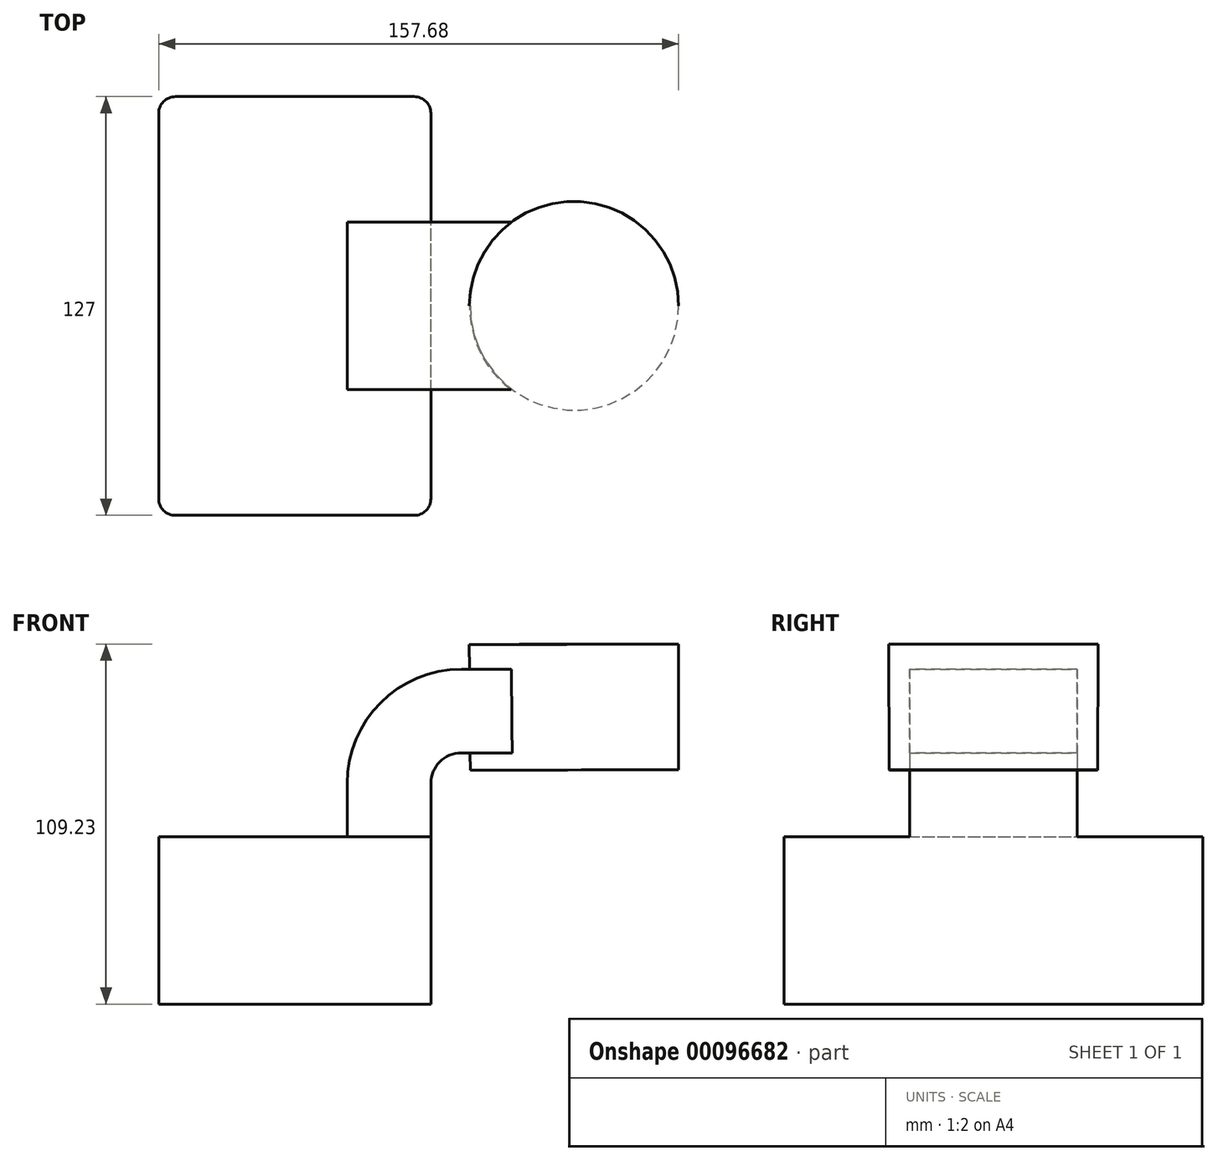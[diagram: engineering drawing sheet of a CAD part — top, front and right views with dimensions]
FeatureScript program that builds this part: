
annotation { "Feature Type Name" : "Feature", "Feature Type Description" : "" }
export const myFeature = defineFeature(function(context is Context, id is Id, definition is map)
    precondition{}
    {
        {
            var Q0;
            Q0=qCreatedBy(makeId("Front.planeOp"),FACE);
            var sketch = newSketch(context, id + "F0", { "sketchPlane" : qUnion([Q0])});
            skLineSegment(sketch, "E0.bottom", {"start": v(41.28, -25.4) * mm, "end": v(-41.27, -25.4) * mm});
            skLineSegment(sketch, "E0.top", {"start": v(41.27, 25.4) * mm, "end": v(-41.28, 25.4) * mm});
            skLineSegment(sketch, "E0.left", {"start": v(41.28, -25.4) * mm, "end": v(41.28, 25.4) * mm});
            skLineSegment(sketch, "E0.right", {"start": v(-41.27, -25.4) * mm, "end": v(-41.28, 25.4) * mm});
            skPoint(sketch, "E0.middle", {"position": v(0, 0) * mm});
            skLineSegment(sketch, "E1.bottom", {"start": v(116.41, 45.73) * mm, "end": v(52.91, 45.73) * mm});
            skLineSegment(sketch, "E1.top", {"start": v(116.41, 83.83) * mm, "end": v(52.91, 83.83) * mm});
            skLineSegment(sketch, "E1.left", {"start": v(116.41, 45.73) * mm, "end": v(116.41, 83.83) * mm});
            skLineSegment(sketch, "E1.right", {"start": v(52.91, 45.73) * mm, "end": v(52.91, 83.83) * mm});
            skPoint(sketch, "E1.middle", {"position": v(84.66, 64.78) * mm});
            skLineSegment(sketch, "E2", {"start": v(41.27, 25.4) * mm, "end": v(41.27, 41.48) * mm});
            skArc(sketch, "E3", {"start": v(41.27, 41.48) * mm, "mid": v(44, 48.07) * mm, "end": v(50.6, 50.8) * mm});
            skLineSegment(sketch, "E4", {"start": v(50.6, 50.8) * mm, "end": v(84.8, 50.8) * mm});
            skLineSegment(sketch, "E5.0", {"start": v(50.6, 76.2) * mm, "end": v(84.8, 76.2) * mm});
            skArc(sketch, "E5.1", {"start": v(15.88, 41.48) * mm, "mid": v(26.05, 66.03) * mm, "end": v(50.6, 76.2) * mm});
            skLineSegment(sketch, "E5.2", {"start": v(15.87, 25.4) * mm, "end": v(15.87, 41.48) * mm});
            skLineSegment(sketch, "E6", {"start": v(84.66, 83.83) * mm, "end": v(84.8, 45.73) * mm});
            skFitSpline(sketch, "E7", {"points": [v(-41.28, 25.4) * mm, v(50.6, 76.2) * mm], "startDerivative": vector(1.94, 80.36) * mm, "endDerivative": vector(144.63, -0.13) * mm});
            skSolve(sketch);
        }
        {
            var Q0;
            Q0=makeQuery(id+"F0.imprint","IMPRINT",FACE,{"disambiguationData":[TD([[makeQuery(id+"F0.imprint","IMPRINT",EDGE,{"derivedFrom":sQuery(id+"F0.wireOp",EDGE,"E0.bottom")}),-1.0]])]});
            extrude(context, id + "F1", {"entities" : qUnion([Q0]), "endBound" : BoundingType.SYMMETRIC, "depth" : 127 * mm});
        }
        {
            var Q0;
            {var subQ1=sQuery(id+"F0.wireOp",EDGE,"E2");Q0=makeQuery(id+"F0.imprint","IMPRINT",FACE,{"disambiguationData":[TD([[makeQuery(id+"F0.imprint","IMPRINT",EDGE,{"derivedFrom":subQ1}),1.0]])]});}
            var Q1;
            {var subQ0=sQuery(id+"F0.wireOp",EDGE,"E4");var subQ1=sQuery(id+"F0.wireOp",EDGE,"E1.right");var subQ2=makeQuery(id+"F0.imprint","INTERSECT",VERTEX,{"derivedFrom":[subQ1,subQ0]});Q1=makeQuery(id+"F0.imprint","IMPRINT",FACE,{"disambiguationData":[TD([[makeQuery(id+"F0.imprint","IMPRINT",EDGE,{"disambiguationData":[TD([[subQ2,-1.0]])],"derivedFrom":subQ1}),-1.0]])]});}
            extrude(context, id + "F2", {"entities" : qUnion([Q0, Q1]), "operationType" : NewBodyOperationType.ADD, "endBound" : BoundingType.SYMMETRIC, "depth" : 50.8 * mm});
        }
        {
            var Q0;
            Q0=makeQuery(id+"F0.imprint","IMPRINT",FACE,{"disambiguationData":[TD([[makeQuery(id+"F0.imprint","IMPRINT",EDGE,{"derivedFrom":sQuery(id+"F0.wireOp",EDGE,"E5.1")}),1.0]])]});
            extrude(context, id + "F3", {"entities" : qUnion([Q0]), "operationType" : NewBodyOperationType.ADD, "endBound" : BoundingType.SYMMETRIC, "depth" : 15.88 * mm});
        }
        {
            var Q0;
            {var subQ0=sQuery(id+"F0.wireOp",EDGE,"E1.left");Q0=makeQuery(id+"F0.imprint","IMPRINT",FACE,{"disambiguationData":[TD([[makeQuery(id+"F0.imprint","IMPRINT",EDGE,{"derivedFrom":subQ0}),1.0]])]});}
            var Q1;
            Q1=sQuery(id+"F0.wireOp",EDGE,"E6");
            revolve(context, id + "F4", {"operationType" : NewBodyOperationType.ADD, "entities" : qUnion([Q0]), "axis" : qUnion([Q1]), "revolveType" : RevolveType.FULL});
        }
        {
            var Q0;
            Q0=makeQuery(id+"F1.opExtrude","CAP_EDGE",EDGE,{"disambiguationData":[OSD([sQuery(id+"F0.wireOp",EDGE,"E0.right")])],"isStart":false});
            var Q1;
            Q1=makeQuery(id+"F1.opExtrude","CAP_EDGE",EDGE,{"disambiguationData":[OSD([sQuery(id+"F0.wireOp",EDGE,"E0.left")])],"isStart":false});
            var Q2;
            Q2=makeQuery(id+"F1.opExtrude","CAP_EDGE",EDGE,{"disambiguationData":[OSD([sQuery(id+"F0.wireOp",EDGE,"E0.right")])],"isStart":true});
            var Q3;
            Q3=makeQuery(id+"F1.opExtrude","CAP_EDGE",EDGE,{"disambiguationData":[OSD([sQuery(id+"F0.wireOp",EDGE,"E0.left")])],"isStart":true});
            fillet(context, id + "F5", {"entities" : qUnion([Q0, Q1, Q2, Q3]), "radius" : 5.08 * mm, "tangentPropagation" : true, "allowEdgeOverflow" : false});
        }
    });
